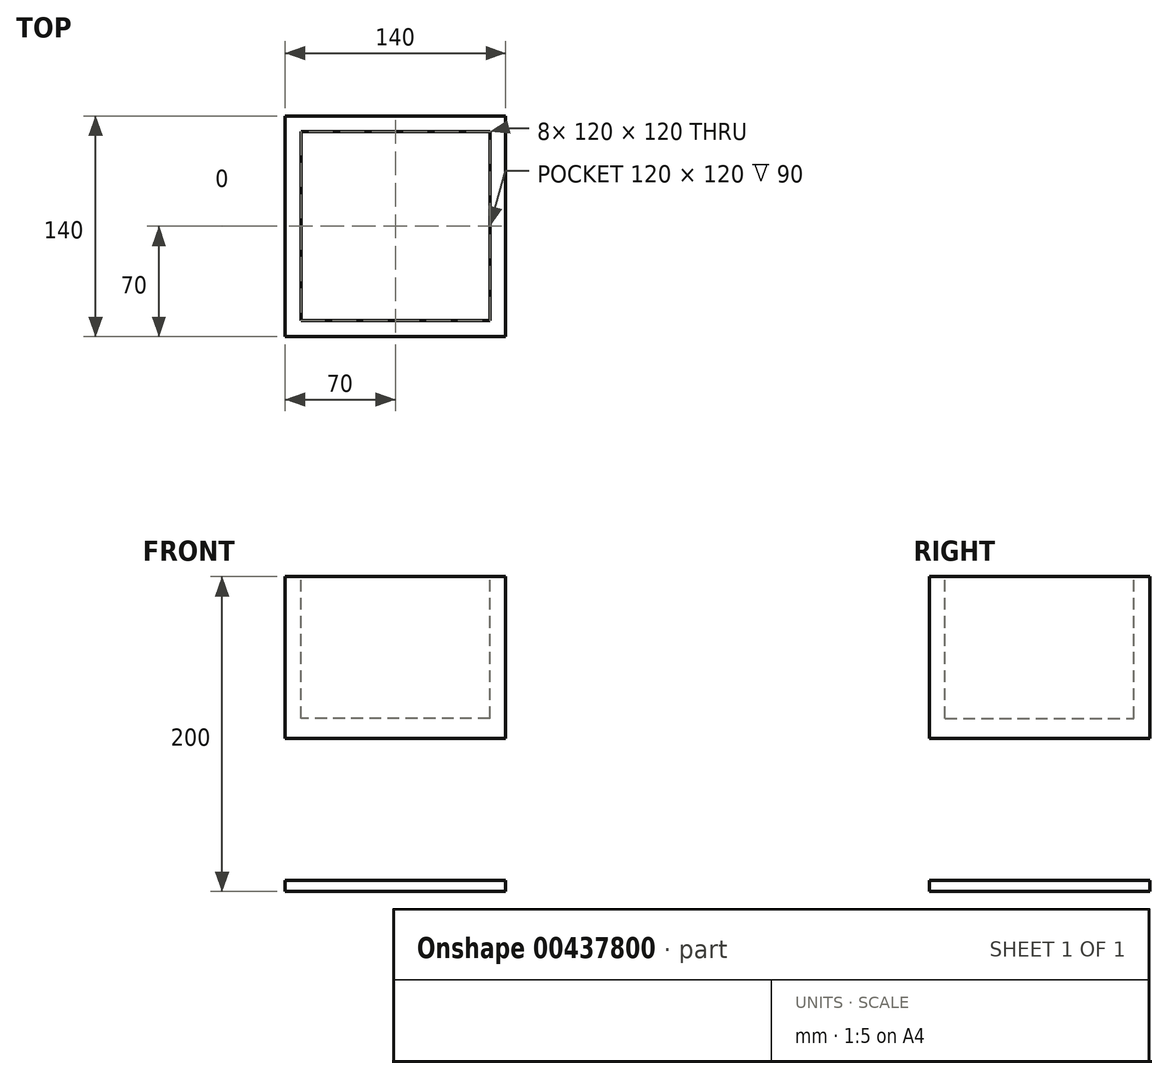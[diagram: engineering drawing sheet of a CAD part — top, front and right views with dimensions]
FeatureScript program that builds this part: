
annotation { "Feature Type Name" : "Feature", "Feature Type Description" : "" }
export const myFeature = defineFeature(function(context is Context, id is Id, definition is map)
    precondition{}
    {
        {
            var Q0;
            Q0=qCreatedBy(makeId("Top.planeOp"),FACE);
            var sketch = newSketch(context, id + "F0", { "sketchPlane" : qUnion([Q0])});
            skLineSegment(sketch, "E0.bottom", {"start": v(70, -70) * mm, "end": v(-70, -70) * mm});
            skLineSegment(sketch, "E0.top", {"start": v(70, 70) * mm, "end": v(-70, 70) * mm});
            skLineSegment(sketch, "E0.left", {"start": v(70, -70) * mm, "end": v(70, 70) * mm});
            skLineSegment(sketch, "E0.right", {"start": v(-70, -70) * mm, "end": v(-70, 70) * mm});
            skPoint(sketch, "E0.middle", {"position": v(0, 0) * mm});
            skSolve(sketch);
        }
        {
            var Q0;
            Q0=makeQuery(id+"F0.imprint","IMPRINT",FACE,{"disambiguationData":[TD([[makeQuery(id+"F0.imprint","IMPRINT",EDGE,{"derivedFrom":sQuery(id+"F0.wireOp",EDGE,"E0.bottom")}),-1.0]])]});
            extrude(context, id + "F1", {"entities" : qUnion([Q0]), "depth" : 200 * mm});
        }
        {
            var Q0;
            Q0=makeQuery(id+"F1.opExtrude","SWEPT_FACE",FACE,{"disambiguationData":[OSD([sQuery(id+"F0.wireOp",EDGE,"E0.top")])]});
            var sketch = newSketch(context, id + "F2", { "sketchPlane" : qUnion([Q0])});
            skLineSegment(sketch, "E1", {"start": v(-70, 100) * mm, "end": v(70, 100) * mm});
            skSolve(sketch);
        }
        {
            var Q0;
            {var subQ0=sQuery(id+"F2.wireOp",EDGE,"E1");Q0=makeQuery(id+"F2.imprint","IMPRINT",FACE,{"disambiguationData":[TD([[makeQuery(id+"F2.imprint","IMPRINT",EDGE,{"derivedFrom":subQ0}),-1.0]])]});}
            var sketch = newSketch(context, id + "F3", { "sketchPlane" : qUnion([Q0])});
            skLineSegment(sketch, "E2.bottom", {"start": v(95, 97.09) * mm, "end": v(-95, 97.09) * mm});
            skLineSegment(sketch, "E2.top", {"start": v(95, 7.09) * mm, "end": v(-95, 7.09) * mm});
            skLineSegment(sketch, "E2.left", {"start": v(95, 97.09) * mm, "end": v(95, 7.09) * mm});
            skLineSegment(sketch, "E2.right", {"start": v(-95, 97.09) * mm, "end": v(-95, 7.09) * mm});
            skPoint(sketch, "E2.middle", {"position": v(0, 52.09) * mm});
            skSolve(sketch);
        }
        {
            var Q0;
            Q0=makeQuery(id+"F3.imprint","IMPRINT",FACE,{"disambiguationData":[TD([[makeQuery(id+"F3.imprint","IMPRINT",EDGE,{"derivedFrom":sQuery(id+"F3.wireOp",EDGE,"E2.bottom")}),1.0]])]});
            extrude(context, id + "F4", {"entities" : qUnion([Q0]), "operationType" : NewBodyOperationType.REMOVE, "oppositeDirection" : true, "depth" : 190 * mm});
        }
        {
            var Q0;
            Q0=makeQuery(id+"F1.opExtrude","CAP_FACE",FACE,{"disambiguationData":[OSD([sQuery(id+"F0.wireOp",EDGE,"E0.bottom"),sQuery(id+"F0.wireOp",EDGE,"E0.top"),sQuery(id+"F0.wireOp",EDGE,"E0.left"),sQuery(id+"F0.wireOp",EDGE,"E0.right")])],"isStart":false});
            var sketch = newSketch(context, id + "F5", { "sketchPlane" : qUnion([Q0])});
            skLineSegment(sketch, "E3.0", {"start": v(60, 60) * mm, "end": v(-60, 60) * mm});
            skLineSegment(sketch, "E3.1", {"start": v(60, -60) * mm, "end": v(60, 60) * mm});
            skLineSegment(sketch, "E3.2", {"start": v(60, -60) * mm, "end": v(-60, -60) * mm});
            skLineSegment(sketch, "E3.3", {"start": v(-60, -60) * mm, "end": v(-60, 60) * mm});
            skSolve(sketch);
        }
        {
            var Q0;
            Q0=makeQuery(id+"F5.imprint","IMPRINT",FACE,{"disambiguationData":[TD([[makeQuery(id+"F5.imprint","IMPRINT",EDGE,{"derivedFrom":sQuery(id+"F5.wireOp",EDGE,"E3.0")}),1.0]])]});
            extrude(context, id + "F6", {"entities" : qUnion([Q0]), "operationType" : NewBodyOperationType.REMOVE, "oppositeDirection" : true, "depth" : 90 * mm});
        }
    });
